# Revit family: Dozownik_mydla_w_płynie_0.5l_POP
name_source: partatom
category: Furniture
units: mm (PartAtom-declared; Revit-internal decimal feet)

## family parameters
Always vertical = Yes
Cut with Voids When Loaded = No
Host = Wall
Room Calculation Point = No
Shared = No

## types (1)
- Type 1
    Color / Kolor = Biały / Szary
    Depth / Glebokosc = 125 mm  [stored 0.410105 ft]
    Description = Dozownik mydła w płynie 0,5 l POP to bardzo trwały i odporny na wszelkie uszkodzenia podajnik mydła. Wykonany jest ze wzmocnionego białego plastiku ABS. Dzięki dużemu, szaremu, ergonomicznemu przyciskowi dozowania jest funkcjonalny i wygodny w użyciu. Dozownik do mydła POP posiada okienko do kontroli ilości mydła. Ma on ATEST  PZH. Zapewnia wysoką jakość w niskiej cenie, dlatego zaspokaja potrzeby nawet najbardziej wymagających użytkowników. Sprawdzi się m.in w szpitalach, hotelach, szkołach, salonach kosmetycznych, restauracjach i biurach.
    Height / Wysokosc = 170 mm  [stored 0.557743 ft]
    Manufacturer = FANECO.com
    Manufacturer code / Kod producenta = 5901764290100
    Material finish / Wykonczenie = Plastic ABS
    Model = POP
    Product code / Kod produktu = S500PGWG
    Type Comments = Dozownik mydła w płynie 0,5 l POP
    URL = https://faneco.com
    Weight / Waga = 0.380 kg
    Width / Szerokosc = 105 mm  [stored 0.344488 ft]

note: [stored X ft] marks values corroborated as IEEE doubles in the binary element streams (Revit-internal decimal feet)

## geometry (parser evidence)
native form markers: Sweep x11
no freeform markers — native parametric forms only
